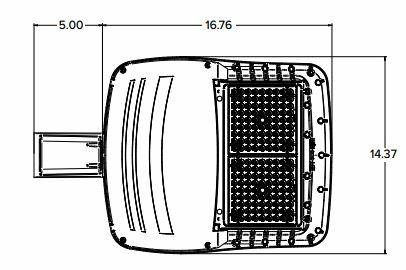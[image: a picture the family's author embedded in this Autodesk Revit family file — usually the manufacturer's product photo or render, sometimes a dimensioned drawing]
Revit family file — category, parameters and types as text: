
# Revit family: VP-2-ADU
name_source: partatom
category: Lighting Fixtures
units: mm (PartAtom-declared; Revit-internal decimal feet)

## family parameters
Cut with Voids When Loaded = No
Host = Face
Light Source = No
OmniClass Number = 23.80.70.11.14.17
OmniClass Title = Direct/Indirect
Part Type = Normal
Room Calculation Point = No
Round Connector Dimension = Use Diameter
Shared = Yes

## types (1)
- VP-2-ADU
    Apparent Load = 168 VA
    Assembly Code = D5020200
    Brand = Beacon
    CRI = 70
    Certification = UL
    Cool Grey = Cool Grey
    Default Elevation = 48 "
    Description = The Viper is an extremely versatile area/site luminaire which blends design, performance, and technology for a variety of applications.
    Features = Featuring two different optical technologies, Micro Strike and Strike Optics, which provide the best distribution patterns for retrofit or new construction
Vibration rated for high vibration applications including bridges and overpasses
Control options including photo control, occupancy sensing, NX Lighting Controls, wiSCAPE and 7-Pin with networked controls
Mounting options include: Arm, Universal Arm, Adjustable Arm, Mast Arm, Decorative Arm, Knuckle, Trunnion, Wall
Distribution options include: Auto Front Row, Type 2, Type 3, Type 4 Forward, Type 4 Wide, Type 5 Narrow, Type 5 Medium, Type 5 Wide, Type 5 Rectangular, Corner Optic, and Tennis Court
    Finish = Arctic White
    Glass = Glass
    Grey = Grey
    Lamp = LED
    Light Output = 12704 cd/m²
    Load Classification = Lighting
    Manufacturer = Current Lighting
    Matt Black = Matt Black
    Matt Grey = MATT GREY
    Matt White = Matt White
    Model = VP-2-ADU
    Name = Viper Area Size 2
    Power Factor = 0.9
    Product Documentation Link = https://cdn.currentlighting.com
    Product Page URL = https://www.currentlighting.com
    Size-2 = SIZE2-ADU
    Type Comments = Lighting Fixture
    URL = https://www.currentlighting.com
    Voltage = 120 V
    Warranty = Five year warranty
    Wattage Comments = 168 W

## geometry (parser evidence)
native form markers: Blend x4, Sweep x5
no freeform markers — native parametric forms only
